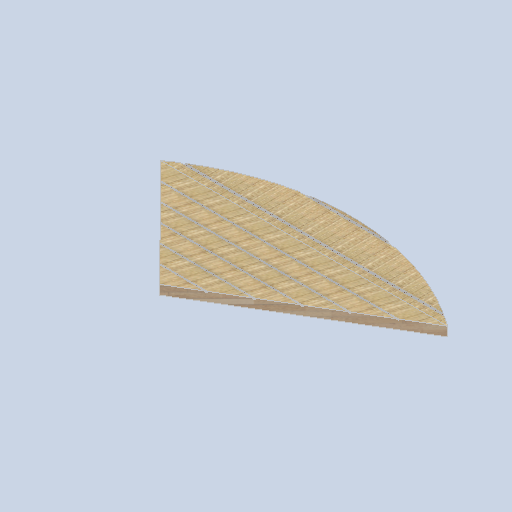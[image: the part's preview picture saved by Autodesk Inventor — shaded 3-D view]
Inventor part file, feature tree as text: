
AUTODESK INVENTOR PART (.ipt)
format: ipt  version: 2024.2 (Build 282272000, 272)  size: 247,808 bytes
history: native  units: in
note: dims shown in document units (in); Inventor stores cm internally (conversion verified against a paired STEP export)
features: sketch x11, plane x4, other x3
ambient origin geometry x8: Origin, YZ Plane, XZ Plane, XY Plane, X Axis, Y Axis, Z Axis, Center Point
bodies: Solid1 (feature_tree)
feature tree (18):
  other  "eave_panel_corner_MIR.ipt"
  other  "Solid1::eave_panel_corner_MIR.ipt"
  other  "TaggingFeature1"
  sketch  "Sketch1"  dims[d0=0.3937in]
  sketch  "Sketch2"
  sketch  "Sketch5"
  sketch  "Sketch6"
  sketch  "Sketch11"
  sketch  "Sketch12"
  sketch  "Sketch13"
  sketch  "Sketch14"
  sketch  "Sketch15"
  sketch  "Sketch16"
  sketch  "Sketch17"
  plane  "Work Plane1"
  plane  "Work Plane2"
  plane  "Work Plane3"
  plane  "Work Plane4"
